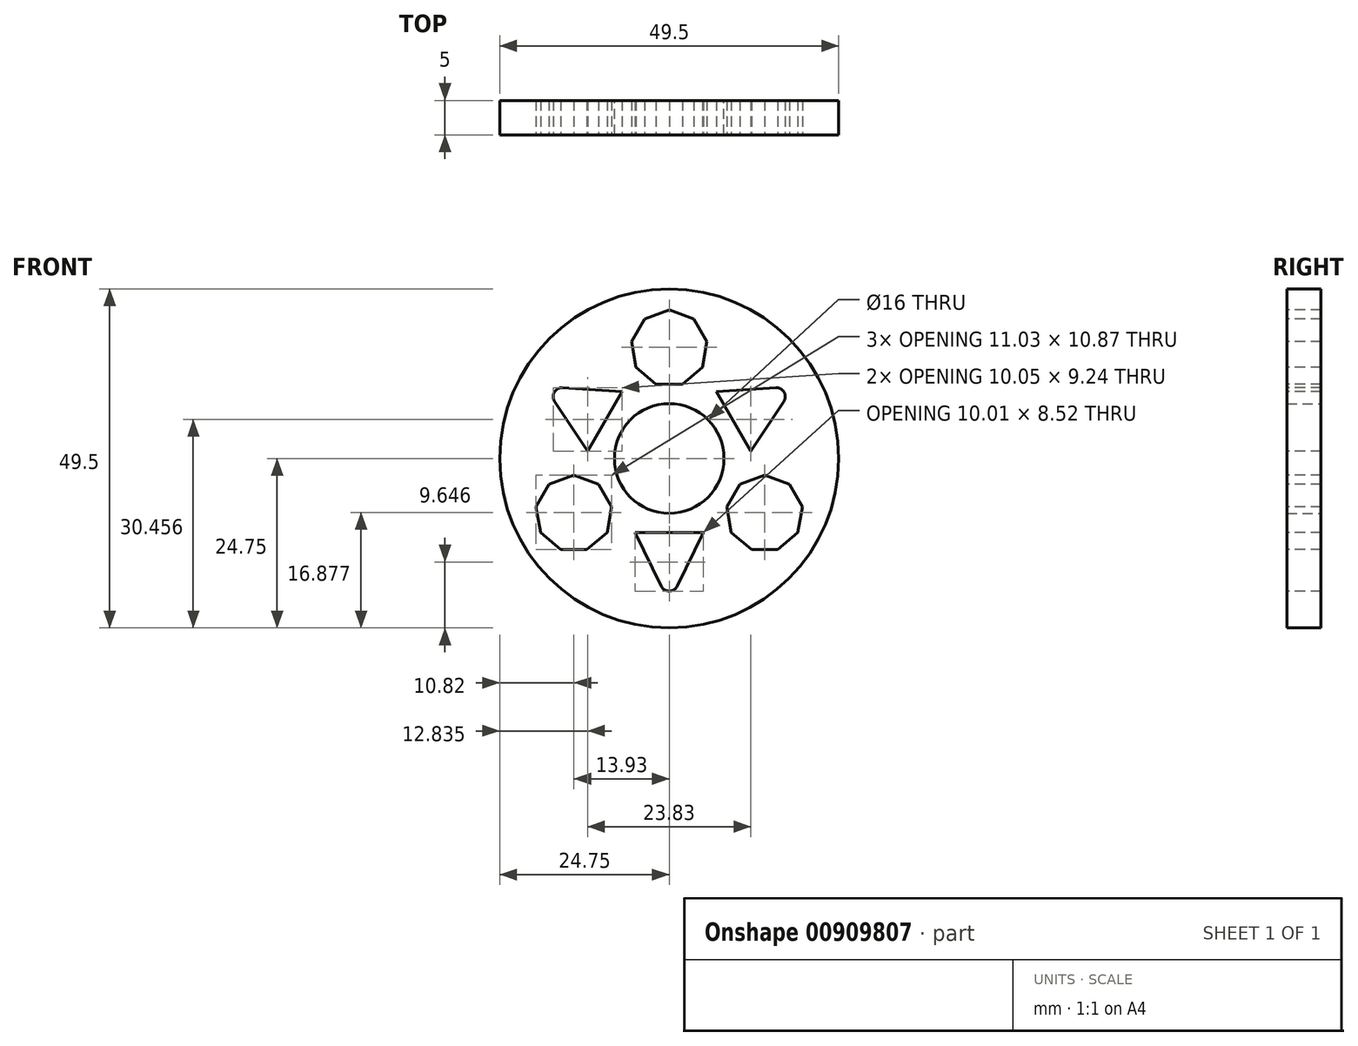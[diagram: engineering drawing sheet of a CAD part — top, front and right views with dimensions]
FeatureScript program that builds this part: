
annotation { "Feature Type Name" : "Feature", "Feature Type Description" : "" }
export const myFeature = defineFeature(function(context is Context, id is Id, definition is map)
    precondition{}
    {
        {
            var Q0;
            Q0=qCreatedBy(makeId("Front.planeOp"),FACE);
            var sketch = newSketch(context, id + "F0", { "sketchPlane" : qUnion([Q0])});
            skCircle(sketch, "E0", {"center": v(0, 0) * mm, "radius": 24.75 * mm});
            skCircle(sketch, "E1", {"center": v(0, 0) * mm, "radius": 8 * mm});
            skSolve(sketch);
        }
        {
            var Q0;
            Q0=makeQuery(id+"F0.imprint","IMPRINT",FACE,{"disambiguationData":[TD([[makeQuery(id+"F0.imprint","IMPRINT",EDGE,{"derivedFrom":sQuery(id+"F0.wireOp",EDGE,"E0")}),1.0]])]});
            extrude(context, id + "F1", {"entities" : qUnion([Q0]), "endBound" : BoundingType.SYMMETRIC, "depth" : 5 * mm, "offsetDistance" : 25.4 * mm});
        }
        {
            var Q0;
            Q0=makeQuery(id+"F1.opExtrude","CAP_FACE",FACE,{"disambiguationData":[OSD([sQuery(id+"F0.wireOp",EDGE,"E0"),sQuery(id+"F0.wireOp",EDGE,"E1")])],"isStart":false});
            var sketch = newSketch(context, id + "F2", { "sketchPlane" : qUnion([Q0])});
            skCircle(sketch, "E2.cCircle", {"center": v(0, 16.08) * mm, "radius": 5.26 * mm, "construction": true});
            skLineSegment(sketch, "E2.0", {"start": v(1.92, 10.82) * mm, "end": v(-1.92, 10.82) * mm});
            skLineSegment(sketch, "E2.1", {"start": v(-1.92, 10.82) * mm, "end": v(-4.85, 13.28) * mm});
            skLineSegment(sketch, "E2.2", {"start": v(-4.85, 13.28) * mm, "end": v(-5.52, 17.06) * mm});
            skLineSegment(sketch, "E2.3", {"start": v(-5.52, 17.06) * mm, "end": v(-3.6, 20.38) * mm});
            skLineSegment(sketch, "E2.4", {"start": v(-3.6, 20.38) * mm, "end": v(0, 21.69) * mm});
            skLineSegment(sketch, "E2.5", {"start": v(0, 21.69) * mm, "end": v(3.6, 20.38) * mm});
            skLineSegment(sketch, "E2.6", {"start": v(3.6, 20.38) * mm, "end": v(5.52, 17.06) * mm});
            skLineSegment(sketch, "E2.7", {"start": v(5.52, 17.06) * mm, "end": v(4.85, 13.28) * mm});
            skLineSegment(sketch, "E2.8", {"start": v(4.85, 13.28) * mm, "end": v(1.92, 10.82) * mm});
            skPoint(sketch, "E2.0.midPoint", {"position": v(0, 10.82) * mm});
            skLineSegment(sketch, "E3.1.0", {"start": v(-18.78, -10.84) * mm, "end": v(-19.45, -7.07) * mm});
            skLineSegment(sketch, "E3.1.1", {"start": v(-15.85, -13.3) * mm, "end": v(-18.78, -10.84) * mm});
            skLineSegment(sketch, "E3.1.2", {"start": v(-12.01, -13.3) * mm, "end": v(-15.85, -13.3) * mm});
            skLineSegment(sketch, "E3.1.3", {"start": v(-9.08, -10.84) * mm, "end": v(-12.01, -13.3) * mm});
            skLineSegment(sketch, "E3.1.4", {"start": v(-8.41, -7.07) * mm, "end": v(-9.08, -10.84) * mm});
            skLineSegment(sketch, "E3.1.5", {"start": v(-10.33, -3.75) * mm, "end": v(-8.41, -7.07) * mm});
            skLineSegment(sketch, "E3.1.6", {"start": v(-13.93, -2.44) * mm, "end": v(-10.33, -3.75) * mm});
            skLineSegment(sketch, "E3.1.7", {"start": v(-17.53, -3.75) * mm, "end": v(-13.93, -2.44) * mm});
            skLineSegment(sketch, "E3.1.8", {"start": v(-19.45, -7.07) * mm, "end": v(-17.53, -3.75) * mm});
            skLineSegment(sketch, "E3.2.0", {"start": v(18.78, -10.84) * mm, "end": v(15.85, -13.3) * mm});
            skLineSegment(sketch, "E3.2.1", {"start": v(19.45, -7.07) * mm, "end": v(18.78, -10.84) * mm});
            skLineSegment(sketch, "E3.2.2", {"start": v(17.53, -3.75) * mm, "end": v(19.45, -7.07) * mm});
            skLineSegment(sketch, "E3.2.3", {"start": v(13.93, -2.44) * mm, "end": v(17.53, -3.75) * mm});
            skLineSegment(sketch, "E3.2.4", {"start": v(10.33, -3.75) * mm, "end": v(13.93, -2.44) * mm});
            skLineSegment(sketch, "E3.2.5", {"start": v(8.41, -7.07) * mm, "end": v(10.33, -3.75) * mm});
            skLineSegment(sketch, "E3.2.6", {"start": v(9.08, -10.84) * mm, "end": v(8.41, -7.07) * mm});
            skLineSegment(sketch, "E3.2.7", {"start": v(12.01, -13.3) * mm, "end": v(9.08, -10.84) * mm});
            skLineSegment(sketch, "E3.2.8", {"start": v(15.85, -13.3) * mm, "end": v(12.01, -13.3) * mm});
            skPoint(sketch, "E3.center", {"position": v(0, 0) * mm});
            skLineSegment(sketch, "E4", {"start": v(1.16, -18.64) * mm, "end": v(5, -10.84) * mm});
            skLineSegment(sketch, "E5", {"start": v(5, -10.84) * mm, "end": v(0, -10.84) * mm});
            skLineSegment(sketch, "E6.MirrorCS", {"start": v(-1.16, -18.64) * mm, "end": v(-5, -10.84) * mm});
            skLineSegment(sketch, "E7.MirrorCS", {"start": v(-5, -10.84) * mm, "end": v(0, -10.84) * mm});
            skLineSegment(sketch, "E8.1.0", {"start": v(11.9, 1.09) * mm, "end": v(9.4, 5.42) * mm});
            skLineSegment(sketch, "E8.1.1", {"start": v(6.89, 9.76) * mm, "end": v(9.4, 5.42) * mm});
            skLineSegment(sketch, "E8.1.2", {"start": v(15.57, 10.33) * mm, "end": v(6.89, 9.76) * mm});
            skLineSegment(sketch, "E8.1.3", {"start": v(16.72, 8.32) * mm, "end": v(11.9, 1.09) * mm});
            skLineSegment(sketch, "E8.2.0", {"start": v(-6.89, 9.76) * mm, "end": v(-9.4, 5.42) * mm});
            skLineSegment(sketch, "E8.2.1", {"start": v(-11.9, 1.09) * mm, "end": v(-9.4, 5.42) * mm});
            skLineSegment(sketch, "E8.2.2", {"start": v(-16.72, 8.32) * mm, "end": v(-11.9, 1.09) * mm});
            skLineSegment(sketch, "E8.2.3", {"start": v(-15.57, 10.33) * mm, "end": v(-6.89, 9.76) * mm});
            skPoint(sketch, "E9.visualSharp", {"position": v(-18.18, 10.5) * mm});
            skArc(sketch, "E9.filletArc", {"start": v(-15.57, 10.33) * mm, "mid": v(-16.77, 9.68) * mm, "end": v(-16.72, 8.32) * mm});
            skPoint(sketch, "E10.visualSharp", {"position": v(18.18, 10.5) * mm});
            skArc(sketch, "E10.filletArc", {"start": v(16.72, 8.32) * mm, "mid": v(16.77, 9.68) * mm, "end": v(15.57, 10.33) * mm});
            skPoint(sketch, "E11.visualSharp", {"position": v(0, -21) * mm});
            skArc(sketch, "E11.filletArc", {"start": v(-1.16, -18.64) * mm, "mid": v(0, -19.36) * mm, "end": v(1.16, -18.64) * mm});
            skSolve(sketch);
        }
        {
            var Q0;
            Q0 = qSketchRegion(id + "F2", true);
            extrude(context, id + "F3", {"entities" : qUnion([Q0]), "operationType" : NewBodyOperationType.REMOVE, "endBound" : BoundingType.THROUGH_ALL, "oppositeDirection" : true, "depth" : 25.4 * mm, "offsetDistance" : 25.4 * mm});
        }
    });
